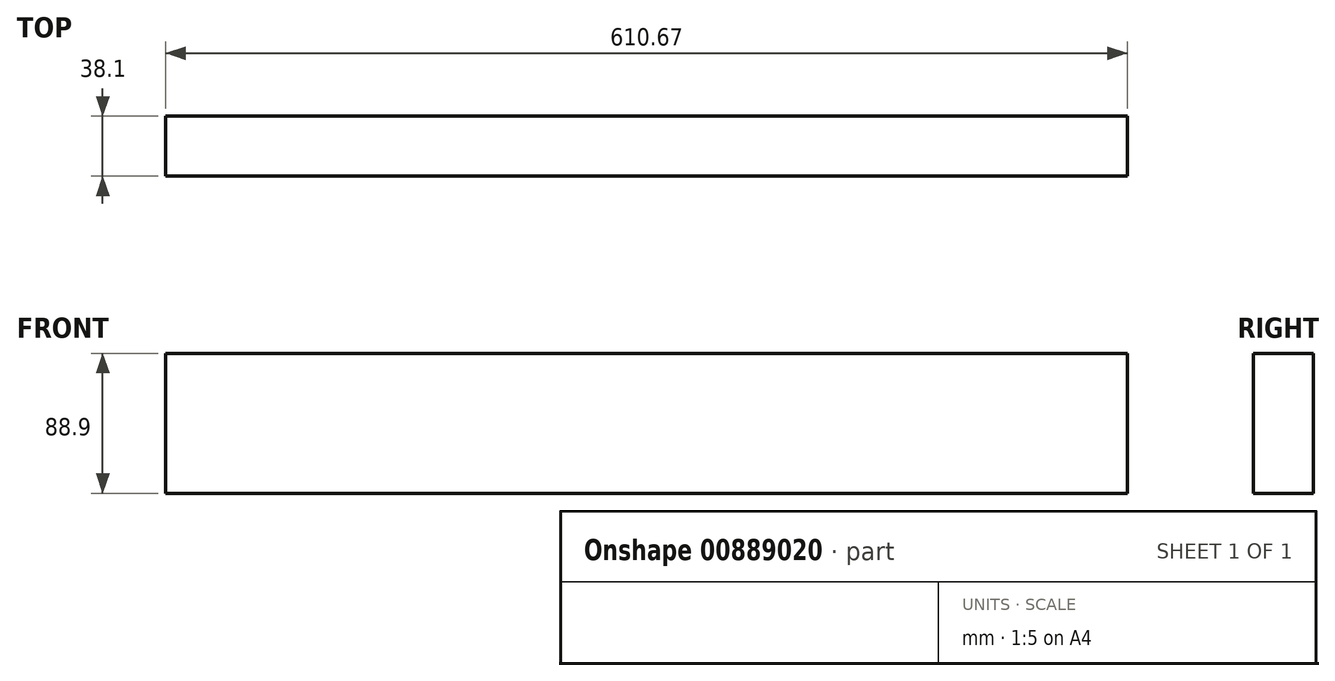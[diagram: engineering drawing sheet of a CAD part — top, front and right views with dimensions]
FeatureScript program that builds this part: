
annotation { "Feature Type Name" : "Feature", "Feature Type Description" : "" }
export const myFeature = defineFeature(function(context is Context, id is Id, definition is map)
    precondition{}
    {
        {
            var Q0;
            Q0=qCreatedBy(makeId("Right.planeOp"),FACE);
            var sketch = newSketch(context, id + "F0", { "sketchPlane" : qUnion([Q0])});
            skLineSegment(sketch, "E0.bottom", {"start": v(-19.05, 44.45) * mm, "end": v(19.05, 44.45) * mm});
            skLineSegment(sketch, "E0.top", {"start": v(-19.05, -44.45) * mm, "end": v(19.05, -44.45) * mm});
            skLineSegment(sketch, "E0.left", {"start": v(-19.05, 44.45) * mm, "end": v(-19.05, -44.45) * mm});
            skLineSegment(sketch, "E0.right", {"start": v(19.05, 44.45) * mm, "end": v(19.05, -44.45) * mm});
            skPoint(sketch, "E0.middle", {"position": v(0, 0) * mm});
            skSolve(sketch);
        }
        {
            var Q0;
            Q0=qSketchRegion(id+"F0",true);
            extrude(context, id + "F1", {"entities" : qUnion([Q0]), "depth" : 610.67 * mm, "offsetDistance" : 25 * mm});
        }
    });
